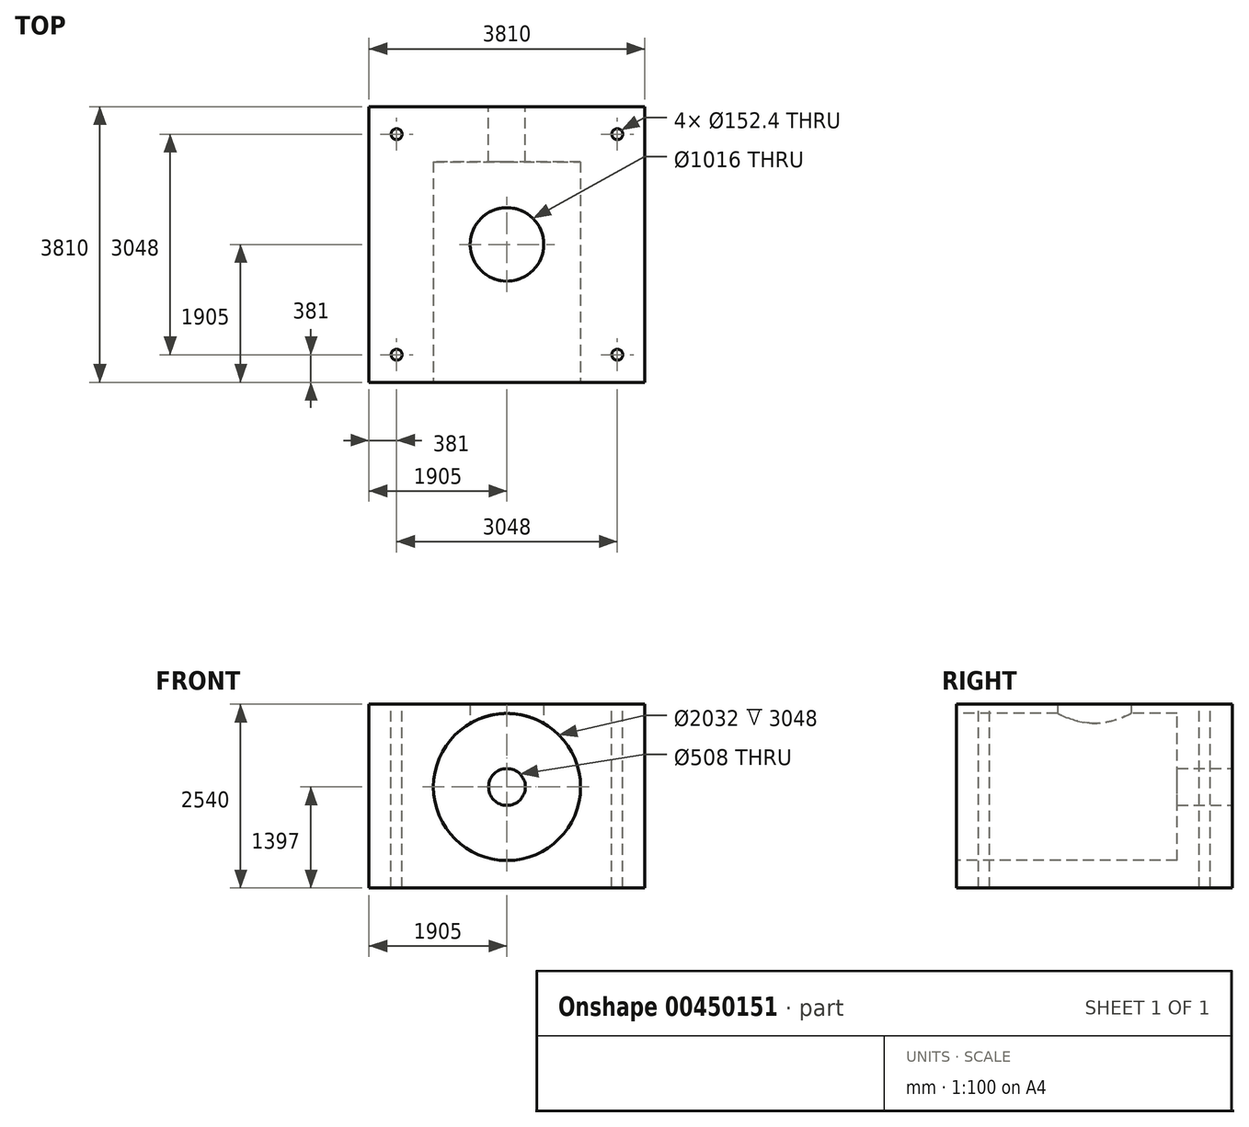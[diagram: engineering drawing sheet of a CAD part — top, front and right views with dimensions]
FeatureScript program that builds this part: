
annotation { "Feature Type Name" : "Feature", "Feature Type Description" : "" }
export const myFeature = defineFeature(function(context is Context, id is Id, definition is map)
    precondition{}
    {
        {
            var Q0;
            Q0=qCreatedBy(makeId("Top.planeOp"),FACE);
            var sketch = newSketch(context, id + "F0", { "sketchPlane" : qUnion([Q0])});
            skLineSegment(sketch, "E0.bottom", {"start": v(0, 0) * mm, "end": v(-3810, 0) * mm});
            skLineSegment(sketch, "E0.top", {"start": v(0, 3810) * mm, "end": v(-3810, 3810) * mm});
            skLineSegment(sketch, "E0.left", {"start": v(0, 0) * mm, "end": v(0, 3810) * mm});
            skLineSegment(sketch, "E0.right", {"start": v(-3810, 0) * mm, "end": v(-3810, 3810) * mm});
            skLineSegment(sketch, "E1", {"start": v(-1905, 0) * mm, "end": v(-1905, 1905) * mm});
            skPoint(sketch, "E1.endSnap0", {"position": v(-1905, 0) * mm});
            skLineSegment(sketch, "E2", {"start": v(-1905, 1905) * mm, "end": v(0, 1905) * mm});
            skCircle(sketch, "E3", {"center": v(-1905, 1905) * mm, "radius": 508 * mm});
            skSolve(sketch);
        }
        {
            var Q0;
            {var subQ1=sQuery(id+"F0.wireOp",EDGE,"E0.left");var subQ6=sQuery(id+"F0.wireOp",EDGE,"E0.bottom");var subQ9=makeQuery(id+"F0.imprint","INTERSECT",VERTEX,{"derivedFrom":[subQ6,subQ1]});Q0=makeQuery(id+"F0.imprint","IMPRINT",FACE,{"disambiguationData":[TD([[makeQuery(id+"F0.imprint","IMPRINT",EDGE,{"disambiguationData":[TD([[subQ9,-1.0]])],"derivedFrom":subQ6}),-1.0]])]});}
            var Q1;
            {var subQ2=sQuery(id+"F0.wireOp",EDGE,"E0.top");Q1=makeQuery(id+"F0.imprint","IMPRINT",FACE,{"disambiguationData":[TD([[makeQuery(id+"F0.imprint","IMPRINT",EDGE,{"derivedFrom":subQ2}),1.0]])]});}
            extrude(context, id + "F1", {"entities" : qUnion([Q0, Q1]), "depth" : 2540 * mm});
        }
        {
            var Q0;
            Q0=makeQuery(id+"F1.opExtrude","CAP_FACE",FACE,{"disambiguationData":[OSD([sQuery(id+"F0.wireOp",EDGE,"E0.bottom"),sQuery(id+"F0.wireOp",EDGE,"E0.top"),sQuery(id+"F0.wireOp",EDGE,"E0.left"),sQuery(id+"F0.wireOp",EDGE,"E0.right"),sQuery(id+"F0.wireOp",EDGE,"E3")])],"isStart":true});
            var sketch = newSketch(context, id + "F2", { "sketchPlane" : qUnion([Q0])});
            skLineSegment(sketch, "E4.bottom", {"start": v(0, 0) * mm, "end": v(-3810, 0) * mm});
            skLineSegment(sketch, "E4.top", {"start": v(0, -3810) * mm, "end": v(-3810, -3810) * mm});
            skLineSegment(sketch, "E4.left", {"start": v(0, 0) * mm, "end": v(0, -3810) * mm});
            skLineSegment(sketch, "E4.right", {"start": v(-3810, 0) * mm, "end": v(-3810, -3810) * mm});
            skSolve(sketch);
        }
        {
            var Q0;
            Q0=makeQuery(id+"F2.imprint","IMPRINT",FACE,{"disambiguationData":[TD([[makeQuery(id+"F2.imprint","IMPRINT",EDGE,{"derivedFrom":makeQuery(id+"F1.opExtrude","CAP_EDGE",EDGE,{"disambiguationData":[OSD([sQuery(id+"F0.wireOp",EDGE,"E3")])],"isStart":true})}),-1.0]])]});
            extrude(context, id + "F3", {"entities" : qUnion([Q0]), "operationType" : NewBodyOperationType.ADD, "depth" : -762 * mm});
        }
        {
            var Q0;
            Q0=makeQuery(id+"F1.opExtrude","SWEPT_FACE",FACE,{"disambiguationData":[OSD([sQuery(id+"F0.wireOp",EDGE,"E0.bottom")])]});
            var sketch = newSketch(context, id + "F4", { "sketchPlane" : qUnion([Q0])});
            skLineSegment(sketch, "E5", {"start": v(-1905, 2540) * mm, "end": v(-1905, 1397) * mm});
            skPoint(sketch, "E5.endSnap0", {"position": v(-1905, 2540) * mm});
            skCircle(sketch, "E6", {"center": v(-1905, 1397) * mm, "radius": 1016 * mm});
            skSolve(sketch);
        }
        {
            var Q0;
            Q0=makeQuery(id+"F4.imprint","IMPRINT",FACE,{"disambiguationData":[TD([[makeQuery(id+"F4.imprint","IMPRINT",EDGE,{"derivedFrom":sQuery(id+"F4.wireOp",EDGE,"E6")}),1.0]])]});
            extrude(context, id + "F5", {"entities" : qUnion([Q0]), "operationType" : NewBodyOperationType.REMOVE, "depth" : -3048 * mm});
        }
        {
            var Q0;
            Q0=makeQuery(id+"F1.opExtrude","SWEPT_FACE",FACE,{"disambiguationData":[OSD([sQuery(id+"F0.wireOp",EDGE,"E0.top")])]});
            var sketch = newSketch(context, id + "F6", { "sketchPlane" : qUnion([Q0])});
            skLineSegment(sketch, "E7", {"start": v(1905, 2540) * mm, "end": v(1905, 1397) * mm});
            skCircle(sketch, "E8", {"center": v(1905, 1397) * mm, "radius": 254 * mm});
            skSolve(sketch);
        }
        {
            var Q0;
            Q0=makeQuery(id+"F6.imprint","IMPRINT",FACE,{"disambiguationData":[TD([[makeQuery(id+"F6.imprint","IMPRINT",EDGE,{"derivedFrom":sQuery(id+"F6.wireOp",EDGE,"E8")}),1.0]])]});
            extrude(context, id + "F7", {"entities" : qUnion([Q0]), "operationType" : NewBodyOperationType.REMOVE, "endBound" : BoundingType.THROUGH_ALL, "oppositeDirection" : true, "depth" : 25.4 * mm});
        }
        {
            var Q0;
            Q0=makeQuery(id+"F5.boolean.opBoolean","COPY",FACE,{"derivedFrom":makeQuery(id+"F5.opExtrude","CAP_FACE",FACE,{"disambiguationData":[OSD([sQuery(id+"F4.wireOp",EDGE,"E6")])],"isStart":false})});
            var sketch = newSketch(context, id + "F8", { "sketchPlane" : qUnion([Q0])});
            skCircle(sketch, "E9", {"center": v(-1905, 1397) * mm, "radius": 508 * mm});
            skSolve(sketch);
        }
        {
            var Q0;
            Q0=makeQuery(id+"F8.imprint","IMPRINT",FACE,{"disambiguationData":[TD([[makeQuery(id+"F8.imprint","IMPRINT",EDGE,{"derivedFrom":makeQuery(id+"F7.boolean.opBoolean","INTERSECT",EDGE,{"derivedFrom":[makeQuery(id+"F5.boolean.opBoolean","COPY",FACE,{"derivedFrom":makeQuery(id+"F5.opExtrude","CAP_FACE",FACE,{"disambiguationData":[OSD([sQuery(id+"F4.wireOp",EDGE,"E6")])],"isStart":false})}),makeQuery(id+"F7.opExtrude","SWEPT_FACE",FACE,{"disambiguationData":[OSD([sQuery(id+"F6.wireOp",EDGE,"E8")])]})]})}),1.0]])]});
            extrude(context, id + "F9", {"entities" : qUnion([Q0]), "operationType" : NewBodyOperationType.REMOVE, "oppositeDirection" : true, "depth" : 508 * mm});
        }
        {
            var Q0;
            Q0=makeQuery(id+"F1.opExtrude","CAP_FACE",FACE,{"disambiguationData":[OSD([sQuery(id+"F0.wireOp",EDGE,"E0.bottom"),sQuery(id+"F0.wireOp",EDGE,"E0.top"),sQuery(id+"F0.wireOp",EDGE,"E0.left"),sQuery(id+"F0.wireOp",EDGE,"E0.right"),sQuery(id+"F0.wireOp",EDGE,"E3")])],"isStart":false});
            var sketch = newSketch(context, id + "F10", { "sketchPlane" : qUnion([Q0])});
            skLineSegment(sketch, "E10", {"start": v(-3810, 3810) * mm, "end": v(-3429, 3810) * mm});
            skLineSegment(sketch, "E11", {"start": v(-3429, 3810) * mm, "end": v(-3429, 3429) * mm});
            skLineSegment(sketch, "E12.left", {"start": v(-3429, 3429) * mm, "end": v(-3429, 3352.8) * mm});
            skCircle(sketch, "E13", {"center": v(-3429, 3429) * mm, "radius": 76.2 * mm});
            skCircle(sketch, "E14", {"center": v(-381, 3429) * mm, "radius": 76.2 * mm});
            skCircle(sketch, "E15", {"center": v(-381, 381) * mm, "radius": 76.2 * mm});
            skCircle(sketch, "E16", {"center": v(-3429, 381) * mm, "radius": 76.2 * mm});
            skLineSegment(sketch, "E17.trimOffspring", {"start": v(-457.2, 3429) * mm, "end": v(-381, 3429) * mm});
            skLineSegment(sketch, "E18.trimOffspring", {"start": v(-3429, 457.2) * mm, "end": v(-3429, 381) * mm});
            skLineSegment(sketch, "E19.trimOffspring", {"start": v(-457.2, 381) * mm, "end": v(-381, 381) * mm});
            skSolve(sketch);
        }
        {
            var Q0;
            {var subQ0=sQuery(id+"F10.wireOp",EDGE,"E12.left");Q0=makeQuery(id+"F10.imprint","IMPRINT",FACE,{"disambiguationData":[TD([[makeQuery(id+"F10.imprint","IMPRINT",EDGE,{"derivedFrom":subQ0}),1.0]])]});}
            var Q1;
            {var subQ0=sQuery(id+"F10.wireOp",EDGE,"E12.left");Q1=makeQuery(id+"F10.imprint","IMPRINT",FACE,{"disambiguationData":[TD([[makeQuery(id+"F10.imprint","IMPRINT",EDGE,{"derivedFrom":subQ0}),-1.0]])]});}
            var Q2;
            Q2=makeQuery(id+"F10.imprint","IMPRINT",FACE,{"disambiguationData":[TD([[makeQuery(id+"F10.imprint","IMPRINT",EDGE,{"derivedFrom":sQuery(id+"F10.wireOp",EDGE,"E14")}),1.0]])]});
            var Q3;
            Q3=makeQuery(id+"F10.imprint","IMPRINT",FACE,{"disambiguationData":[TD([[makeQuery(id+"F10.imprint","IMPRINT",EDGE,{"derivedFrom":sQuery(id+"F10.wireOp",EDGE,"E15")}),1.0]])]});
            var Q4;
            Q4=makeQuery(id+"F10.imprint","IMPRINT",FACE,{"disambiguationData":[TD([[makeQuery(id+"F10.imprint","IMPRINT",EDGE,{"derivedFrom":sQuery(id+"F10.wireOp",EDGE,"E16")}),1.0]])]});
            extrude(context, id + "F11", {"entities" : qUnion([Q0, Q1, Q2, Q3, Q4]), "operationType" : NewBodyOperationType.REMOVE, "endBound" : BoundingType.THROUGH_ALL, "oppositeDirection" : true, "depth" : 25.4 * mm});
        }
    });
